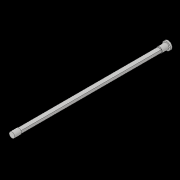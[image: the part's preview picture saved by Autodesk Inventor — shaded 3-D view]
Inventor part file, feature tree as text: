
AUTODESK INVENTOR PART (.ipt)
format: ipt  version: 2017 (Build 210142000, 142)  size: 93,696 bytes
history: native  units: in
note: dims shown in document units (in); Inventor stores cm internally (conversion verified against a paired STEP export)
features: extrude x4, sketch x4
ambient origin geometry x8: Origin, YZ Plane, XZ Plane, XY Plane, X Axis, Y Axis, Z Axis, Center Point
bodies: Solid1 (feature_tree)
feature tree (8):
  extrude  "Extrusion1"  Depth=0.2in
  extrude  "Extrusion2"  Depth=10.229in
  extrude  "Extrusion3"  Depth=0.1499in
  extrude  "Extrusion4"  Depth=0.125in
  sketch  "Sketch1"  dims[d0=0.3in d1=0.2in]
  sketch  "Sketch2"  dims[d2=10.229in d3=0.0in d4=0.4in]
  sketch  "Sketch3"  dims[d5=0.1in d6=0.1499in]
  sketch  "Sketch4"  dims[d7=0.5in d8=0.0in d9=0.4in d10=0.5in d11=0.0in d12=0.6in d13=0.125in d14=0.0in]
